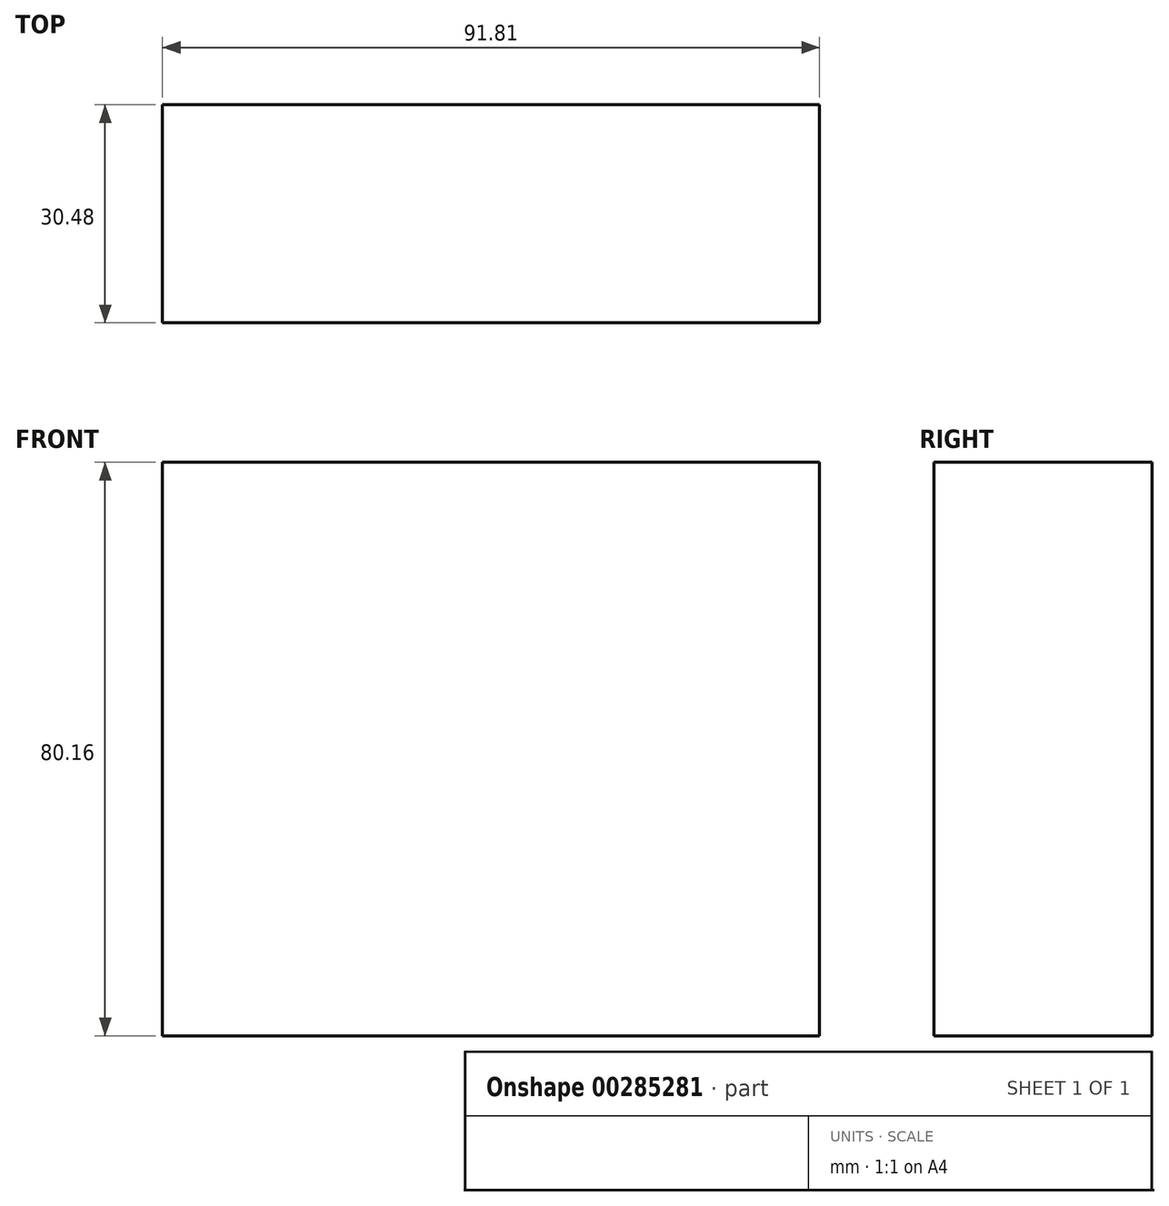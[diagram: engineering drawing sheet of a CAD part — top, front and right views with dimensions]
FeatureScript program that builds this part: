
annotation { "Feature Type Name" : "Feature", "Feature Type Description" : "" }
export const myFeature = defineFeature(function(context is Context, id is Id, definition is map)
    precondition{}
    {
        {
            var Q0;
            Q0=qCreatedBy(makeId("Front.planeOp"),FACE);
            var sketch = newSketch(context, id + "F0", { "sketchPlane" : qUnion([Q0])});
            skLineSegment(sketch, "E0", {"start": v(-47.8, 30.75) * mm, "end": v(-47.8, -49.4) * mm});
            skLineSegment(sketch, "E1", {"start": v(-47.8, -49.4) * mm, "end": v(44.01, -49.4) * mm});
            skLineSegment(sketch, "E2", {"start": v(44.01, -49.4) * mm, "end": v(44.01, 30.75) * mm});
            skLineSegment(sketch, "E3", {"start": v(44.01, 30.75) * mm, "end": v(-47.8, 30.75) * mm});
            skSolve(sketch);
        }
        {
            var Q0;
            Q0 = qSketchRegion(id + "F0", true);
            extrude(context, id + "F1", {"entities" : qUnion([Q0]), "depth" : 30.48 * mm});
        }
    });
